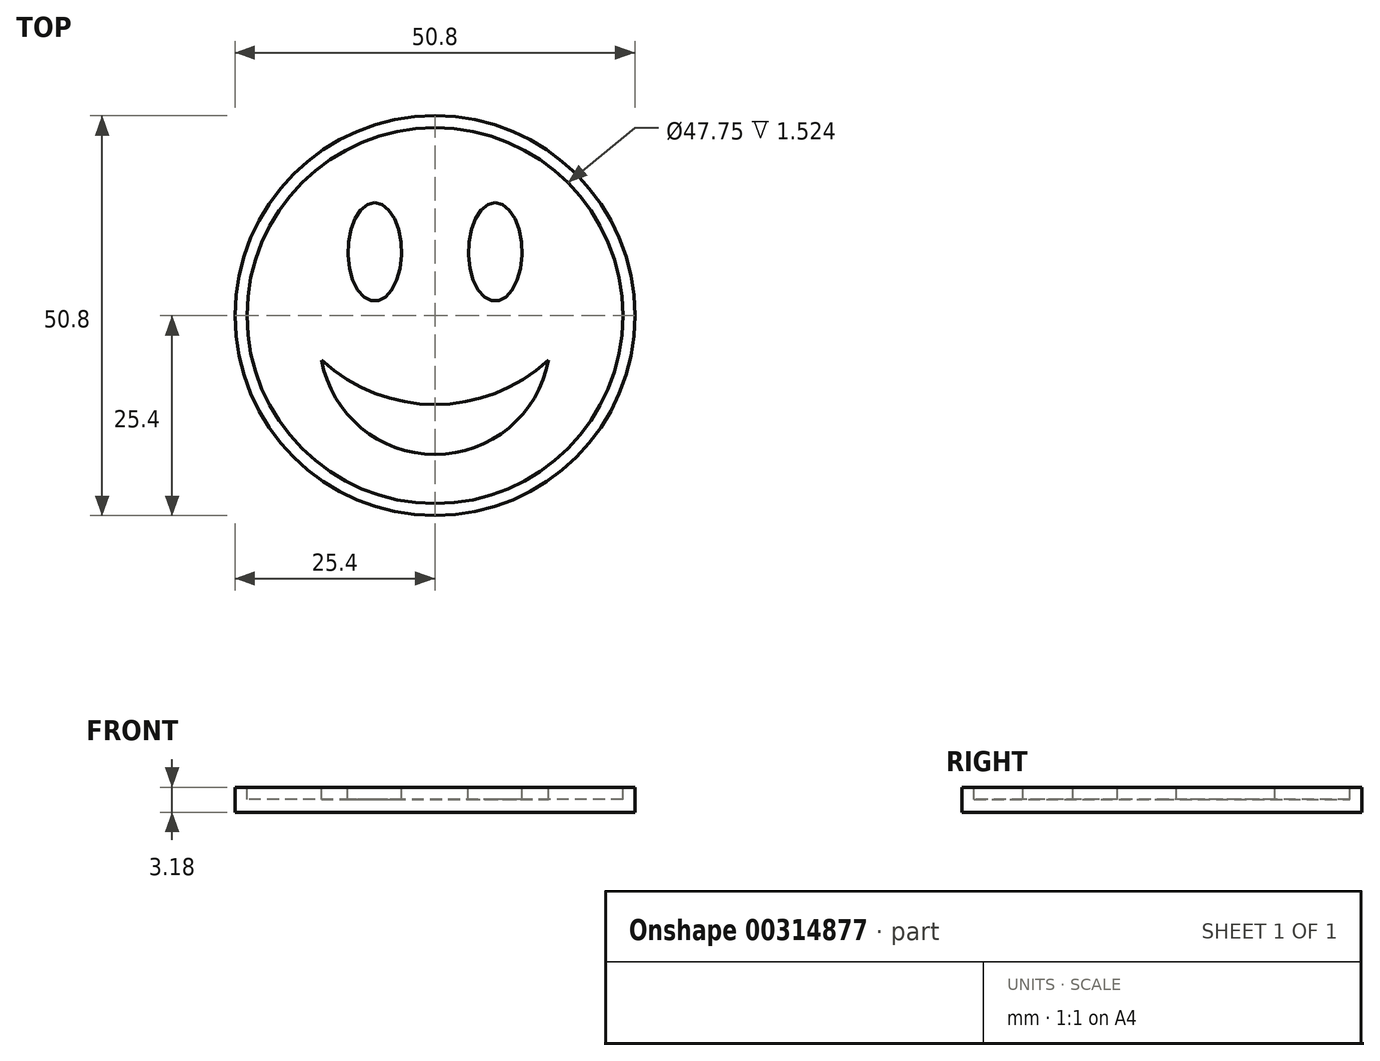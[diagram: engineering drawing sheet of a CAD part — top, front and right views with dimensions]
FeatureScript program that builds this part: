
annotation { "Feature Type Name" : "Feature", "Feature Type Description" : "" }
export const myFeature = defineFeature(function(context is Context, id is Id, definition is map)
    precondition{}
    {
        {
            var Q0;
            Q0=qCreatedBy(makeId("Top.planeOp"),FACE);
            var sketch = newSketch(context, id + "F0", { "sketchPlane" : qUnion([Q0])});
            skCircle(sketch, "E0", {"center": v(0, 0) * mm, "radius": 25.4 * mm});
            skSolve(sketch);
        }
        {
            var Q0;
            Q0=makeQuery(id+"F0.imprint","IMPRINT",FACE,{"disambiguationData":[TD([[makeQuery(id+"F0.imprint","IMPRINT",EDGE,{"derivedFrom":sQuery(id+"F0.wireOp",EDGE,"E0")}),1.0]])]});
            extrude(context, id + "F1", {"entities" : qUnion([Q0]), "depth" : 3.17 * mm});
        }
        {
            var Q0;
            Q0=makeQuery(id+"F1.opExtrude","CAP_FACE",FACE,{"disambiguationData":[OSD([sQuery(id+"F0.wireOp",EDGE,"E0")])],"isStart":false});
            var sketch = newSketch(context, id + "F2", { "sketchPlane" : qUnion([Q0])});
            skEllipse(sketch, "E1", {"center": v(-7.65, 8.1) * mm, "majorRadius": 6.24 * mm, "minorRadius": 3.42 * mm, "majorAxis": v(0, 1)});
            skArc(sketch, "E2", {"start": v(-14.42, -5.63) * mm, "mid": v(0, -17.64) * mm, "end": v(14.42, -5.63) * mm});
            skArc(sketch, "E3", {"start": v(-14.42, -5.63) * mm, "mid": v(0, -11.29) * mm, "end": v(14.42, -5.63) * mm});
            skEllipse(sketch, "E4.MirrorC", {"center": v(7.65, 8.1) * mm, "majorRadius": 6.24 * mm, "minorRadius": 3.42 * mm, "majorAxis": v(0, 1)});
            skCircle(sketch, "E5", {"center": v(0, 0) * mm, "radius": 23.88 * mm});
            skSolve(sketch);
        }
        {
            var Q0;
            Q0=makeQuery(id+"F2.imprint","IMPRINT",FACE,{"disambiguationData":[TD([[makeQuery(id+"F2.imprint","IMPRINT",EDGE,{"derivedFrom":sQuery(id+"F2.wireOp",EDGE,"E1")}),-1.0]])]});
            extrude(context, id + "F3", {"entities" : qUnion([Q0]), "operationType" : NewBodyOperationType.REMOVE, "oppositeDirection" : true, "depth" : 1.52 * mm});
        }
    });
